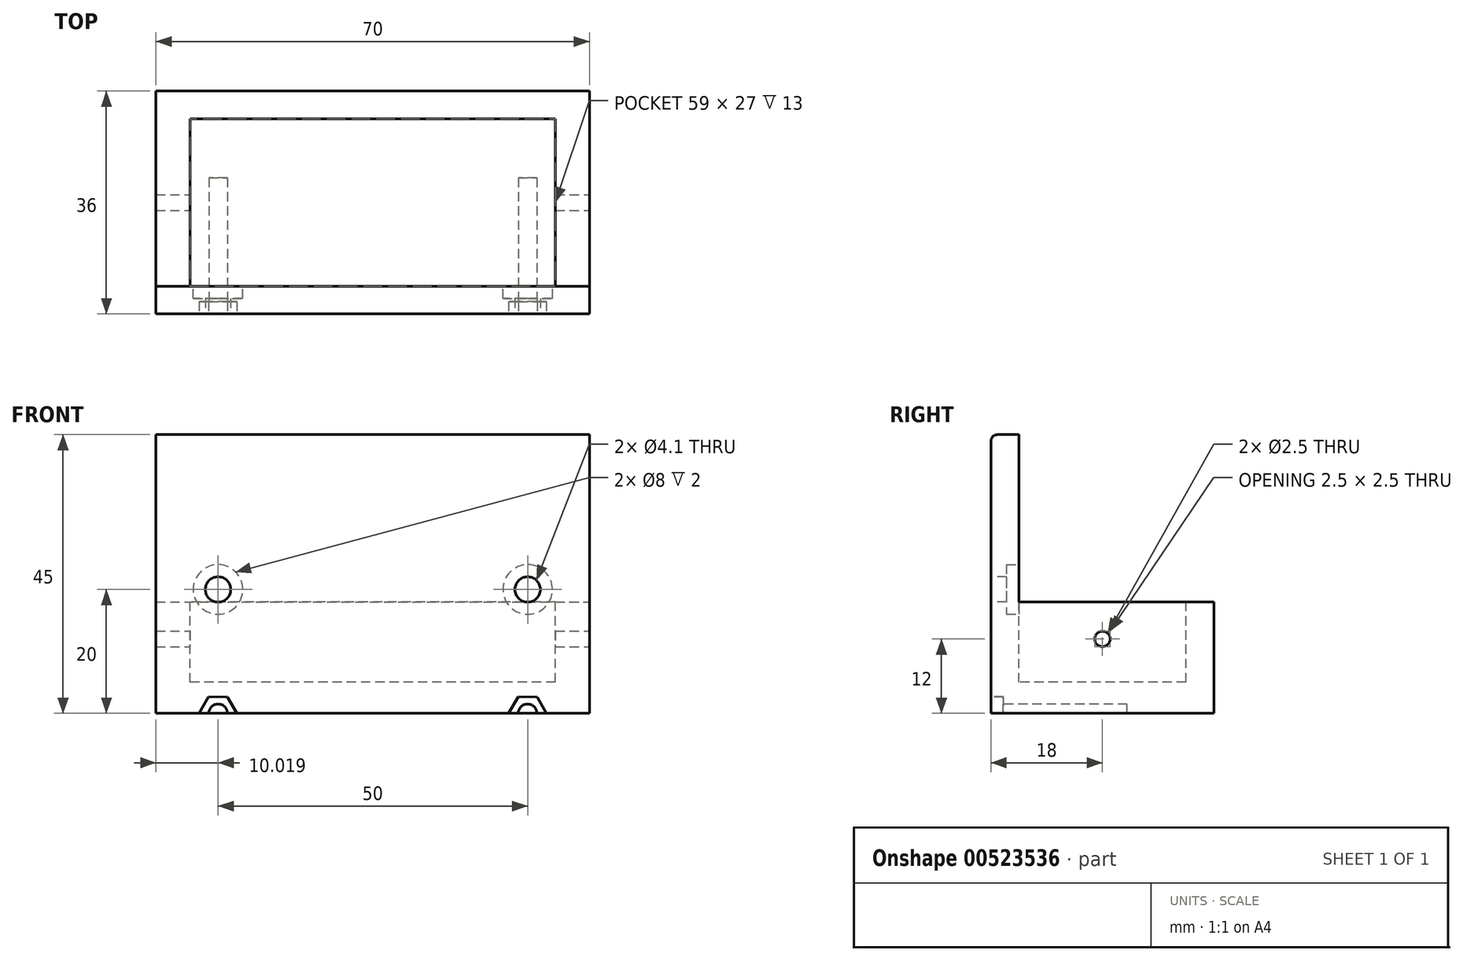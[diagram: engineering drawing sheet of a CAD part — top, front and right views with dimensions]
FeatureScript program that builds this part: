
annotation { "Feature Type Name" : "Feature", "Feature Type Description" : "" }
export const myFeature = defineFeature(function(context is Context, id is Id, definition is map)
    precondition{}
    {
        {
            var Q0;
            Q0=qCreatedBy(makeId("Top.planeOp"),FACE);
            var sketch = newSketch(context, id + "F0", { "sketchPlane" : qUnion([Q0])});
            skLineSegment(sketch, "E0.bottom", {"start": v(35, 18) * mm, "end": v(-35, 18) * mm});
            skLineSegment(sketch, "E0.top", {"start": v(35, -18) * mm, "end": v(-35, -18) * mm});
            skLineSegment(sketch, "E0.left", {"start": v(35, 18) * mm, "end": v(35, -18) * mm});
            skLineSegment(sketch, "E0.right", {"start": v(-35, 18) * mm, "end": v(-35, -18) * mm});
            skPoint(sketch, "E0.middle", {"position": v(0, 0) * mm});
            skSolve(sketch);
        }
        {
            var Q0;
            Q0=makeQuery(id+"F0.imprint","IMPRINT",FACE,{"disambiguationData":[TD([[makeQuery(id+"F0.imprint","IMPRINT",EDGE,{"derivedFrom":sQuery(id+"F0.wireOp",EDGE,"E0.bottom")}),1.0]])]});
            extrude(context, id + "F1", {"entities" : qUnion([Q0]), "depth" : 45 * mm, "offsetDistance" : 25.4 * mm});
        }
        {
            var Q0;
            Q0=makeQuery(id+"F1.opExtrude","CAP_FACE",FACE,{"disambiguationData":[OSD([sQuery(id+"F0.wireOp",EDGE,"E0.bottom"),sQuery(id+"F0.wireOp",EDGE,"E0.top"),sQuery(id+"F0.wireOp",EDGE,"E0.left"),sQuery(id+"F0.wireOp",EDGE,"E0.right")])],"isStart":false});
            var sketch = newSketch(context, id + "F2", { "sketchPlane" : qUnion([Q0])});
            skLineSegment(sketch, "E1.bottom", {"start": v(29.5, 13.5) * mm, "end": v(-29.5, 13.5) * mm});
            skLineSegment(sketch, "E1.top", {"start": v(29.5, -13.5) * mm, "end": v(-29.5, -13.5) * mm});
            skLineSegment(sketch, "E1.left", {"start": v(29.5, 13.5) * mm, "end": v(29.5, -13.5) * mm});
            skLineSegment(sketch, "E1.right", {"start": v(-29.5, 13.5) * mm, "end": v(-29.5, -13.5) * mm});
            skPoint(sketch, "E1.middle", {"position": v(0, 0) * mm});
            skSolve(sketch);
        }
        {
            var Q0;
            Q0=makeQuery(id+"F2.imprint","IMPRINT",FACE,{"disambiguationData":[TD([[makeQuery(id+"F2.imprint","IMPRINT",EDGE,{"derivedFrom":sQuery(id+"F2.wireOp",EDGE,"E1.bottom")}),1.0]])]});
            extrude(context, id + "F3", {"entities" : qUnion([Q0]), "operationType" : NewBodyOperationType.REMOVE, "oppositeDirection" : true, "depth" : 40 * mm, "offsetDistance" : 25.4 * mm});
        }
        {
            var Q0;
            Q0=makeQuery(id+"F1.opExtrude","SWEPT_FACE",FACE,{"disambiguationData":[OSD([sQuery(id+"F0.wireOp",EDGE,"E0.left")])]});
            var sketch = newSketch(context, id + "F4", { "sketchPlane" : qUnion([Q0])});
            skLineSegment(sketch, "E2.bottom", {"start": v(-13.5, 45) * mm, "end": v(18.02, 45) * mm});
            skLineSegment(sketch, "E2.top", {"start": v(-13.5, 18) * mm, "end": v(18.02, 18) * mm});
            skLineSegment(sketch, "E2.left", {"start": v(-13.5, 45) * mm, "end": v(-13.5, 18) * mm});
            skLineSegment(sketch, "E2.right", {"start": v(18.02, 45) * mm, "end": v(18.02, 18) * mm});
            skSolve(sketch);
        }
        {
            var Q0;
            Q0=makeQuery(id+"F4.imprint","IMPRINT",FACE,{"disambiguationData":[TD([[makeQuery(id+"F4.imprint","IMPRINT",EDGE,{"derivedFrom":sQuery(id+"F4.wireOp",EDGE,"E2.bottom")}),1.0]])]});
            extrude(context, id + "F5", {"entities" : qUnion([Q0]), "operationType" : NewBodyOperationType.REMOVE, "endBound" : BoundingType.THROUGH_ALL, "oppositeDirection" : true, "depth" : 25.4 * mm, "offsetDistance" : 25.4 * mm});
        }
        {
            var Q0;
            Q0=makeQuery(id+"F1.opExtrude","SWEPT_FACE",FACE,{"disambiguationData":[OSD([sQuery(id+"F0.wireOp",EDGE,"E0.left")])]});
            var sketch = newSketch(context, id + "F6", { "sketchPlane" : qUnion([Q0])});
            skCircle(sketch, "E3", {"center": v(0, 12) * mm, "radius": 1.25 * mm});
            skSolve(sketch);
        }
        {
            var Q0;
            Q0=makeQuery(id+"F6.imprint","IMPRINT",FACE,{"disambiguationData":[TD([[makeQuery(id+"F6.imprint","IMPRINT",EDGE,{"derivedFrom":sQuery(id+"F6.wireOp",EDGE,"E3")}),1.0]])]});
            extrude(context, id + "F7", {"entities" : qUnion([Q0]), "operationType" : NewBodyOperationType.REMOVE, "endBound" : BoundingType.THROUGH_ALL, "oppositeDirection" : true, "depth" : 25.4 * mm, "offsetDistance" : 25.4 * mm});
        }
        {
            var Q0;
            Q0=makeQuery(id+"F1.opExtrude","SWEPT_FACE",FACE,{"disambiguationData":[OSD([sQuery(id+"F0.wireOp",EDGE,"E0.top")])]});
            var sketch = newSketch(context, id + "F8", { "sketchPlane" : qUnion([Q0])});
            skPoint(sketch, "E4", {"position": v(0, 0) * mm});
            skCircle(sketch, "E5.cCircle", {"center": v(25, 0) * mm, "radius": 2.64 * mm, "construction": true});
            skLineSegment(sketch, "E5.0", {"start": v(23.46, -2.63) * mm, "end": v(21.95, 0.02) * mm});
            skLineSegment(sketch, "E5.1", {"start": v(21.95, 0.02) * mm, "end": v(23.5, 2.65) * mm});
            skLineSegment(sketch, "E5.2", {"start": v(23.5, 2.65) * mm, "end": v(26.54, 2.63) * mm});
            skLineSegment(sketch, "E5.3", {"start": v(26.54, 2.63) * mm, "end": v(28.05, -0.02) * mm});
            skLineSegment(sketch, "E5.4", {"start": v(28.05, -0.02) * mm, "end": v(26.5, -2.65) * mm});
            skLineSegment(sketch, "E5.5", {"start": v(26.5, -2.65) * mm, "end": v(23.46, -2.63) * mm});
            skPoint(sketch, "E5.0.midPoint", {"position": v(22.7, -1.3) * mm});
            skCircle(sketch, "E6.cCircle", {"center": v(-25, 0) * mm, "radius": 2.64 * mm, "construction": true});
            skLineSegment(sketch, "E6.0", {"start": v(-26.54, -2.63) * mm, "end": v(-28.05, 0.02) * mm});
            skLineSegment(sketch, "E6.1", {"start": v(-28.05, 0.02) * mm, "end": v(-26.5, 2.65) * mm});
            skLineSegment(sketch, "E6.2", {"start": v(-26.5, 2.65) * mm, "end": v(-23.46, 2.63) * mm});
            skLineSegment(sketch, "E6.3", {"start": v(-23.46, 2.63) * mm, "end": v(-21.95, -0.02) * mm});
            skLineSegment(sketch, "E6.4", {"start": v(-21.95, -0.02) * mm, "end": v(-23.5, -2.65) * mm});
            skLineSegment(sketch, "E6.5", {"start": v(-23.5, -2.65) * mm, "end": v(-26.54, -2.63) * mm});
            skPoint(sketch, "E6.0.midPoint", {"position": v(-27.3, -1.3) * mm});
            skSolve(sketch);
        }
        {
            var Q0;
            {var subQ6=sQuery(id+"F8.wireOp",EDGE,"E6.1");Q0=makeQuery(id+"F8.imprint","IMPRINT",FACE,{"disambiguationData":[TD([[makeQuery(id+"F8.imprint","IMPRINT",EDGE,{"derivedFrom":subQ6}),-1.0]])]});}
            var Q1;
            {var subQ4=sQuery(id+"F8.wireOp",EDGE,"E5.1");Q1=makeQuery(id+"F8.imprint","IMPRINT",FACE,{"disambiguationData":[TD([[makeQuery(id+"F8.imprint","IMPRINT",EDGE,{"derivedFrom":subQ4}),-1.0]])]});}
            extrude(context, id + "F9", {"entities" : qUnion([Q0, Q1]), "operationType" : NewBodyOperationType.REMOVE, "oppositeDirection" : true, "depth" : 2 * mm, "offsetDistance" : 25.4 * mm});
        }
        {
            var Q0;
            Q0=makeQuery(id+"F9.boolean.opBoolean","COPY",FACE,{"derivedFrom":makeQuery(id+"F9.opExtrude","CAP_FACE",FACE,{"disambiguationData":[OSD([sQuery(id+"F0.wireOp",EDGE,"E0.top"),sQuery(id+"F8.wireOp",EDGE,"E5.0"),sQuery(id+"F8.wireOp",EDGE,"E5.1"),sQuery(id+"F8.wireOp",EDGE,"E5.2"),sQuery(id+"F8.wireOp",EDGE,"E5.3")])],"isStart":false})});
            var sketch = newSketch(context, id + "F10", { "sketchPlane" : qUnion([Q0])});
            skCircle(sketch, "E7", {"center": v(25, 0) * mm, "radius": 1.5 * mm});
            skCircle(sketch, "E8", {"center": v(-24.97, 0) * mm, "radius": 1.5 * mm});
            skSolve(sketch);
        }
        {
            var Q0;
            {var subQ0=sQuery(id+"F10.wireOp",EDGE,"E7");var subQ1=sQuery(id+"F0.wireOp",EDGE,"E0.top");var subQ2=makeQuery(id+"F1.opExtrude","CAP_EDGE",EDGE,{"disambiguationData":[OSD([subQ1])],"isStart":true});var subQ3=makeQuery(id+"F9.boolean.opBoolean","COPY",EDGE,{"derivedFrom":makeQuery(id+"F9.opExtrude","CAP_EDGE",EDGE,{"disambiguationData":[OSD([subQ1]),TDD([makeQuery(id+"F8.imprint","IMPRINT",EDGE,{"disambiguationData":[TD([[makeQuery(id+"F8.imprint","INTERSECT",VERTEX,{"derivedFrom":[subQ2,sQuery(id+"F8.wireOp",EDGE,"E5.0")]}),1.0]])],"derivedFrom":subQ2})])],"isStart":false})});var subQ4=makeQuery(id+"F10.imprint","INTERSECT",VERTEX,{"disambiguationData":[OD(0.0)],"derivedFrom":[subQ3,subQ0]});Q0=makeQuery(id+"F10.imprint","IMPRINT",FACE,{"disambiguationData":[TD([[makeQuery(id+"F10.imprint","IMPRINT",EDGE,{"disambiguationData":[TD([[subQ4,-1.0]])],"derivedFrom":subQ0}),1.0]])]});}
            var Q1;
            {var subQ0=sQuery(id+"F10.wireOp",EDGE,"E7");var subQ1=sQuery(id+"F0.wireOp",EDGE,"E0.top");var subQ2=makeQuery(id+"F1.opExtrude","CAP_EDGE",EDGE,{"disambiguationData":[OSD([subQ1])],"isStart":true});var subQ3=makeQuery(id+"F9.boolean.opBoolean","COPY",EDGE,{"derivedFrom":makeQuery(id+"F9.opExtrude","CAP_EDGE",EDGE,{"disambiguationData":[OSD([subQ1]),TDD([makeQuery(id+"F8.imprint","IMPRINT",EDGE,{"disambiguationData":[TD([[makeQuery(id+"F8.imprint","INTERSECT",VERTEX,{"derivedFrom":[subQ2,sQuery(id+"F8.wireOp",EDGE,"E5.0")]}),1.0]])],"derivedFrom":subQ2})])],"isStart":false})});var subQ4=makeQuery(id+"F10.imprint","INTERSECT",VERTEX,{"disambiguationData":[OD(0.0)],"derivedFrom":[subQ3,subQ0]});Q1=makeQuery(id+"F10.imprint","IMPRINT",FACE,{"disambiguationData":[TD([[makeQuery(id+"F10.imprint","IMPRINT",EDGE,{"disambiguationData":[TD([[subQ4,1.0]])],"derivedFrom":subQ0}),1.0]])]});}
            var Q2;
            Q2=makeQuery(id+"F10.imprint","IMPRINT",FACE,{"disambiguationData":[TD([[makeQuery(id+"F10.imprint","IMPRINT",EDGE,{"derivedFrom":sQuery(id+"F10.wireOp",EDGE,"E8")}),1.0]])]});
            extrude(context, id + "F11", {"entities" : qUnion([Q0, Q1, Q2]), "operationType" : NewBodyOperationType.REMOVE, "oppositeDirection" : true, "depth" : 20 * mm, "offsetDistance" : 25.4 * mm});
        }
        {
            var Q0;
            Q0=makeQuery(id+"F1.opExtrude","SWEPT_FACE",FACE,{"disambiguationData":[OSD([sQuery(id+"F0.wireOp",EDGE,"E0.top")])]});
            var sketch = newSketch(context, id + "F12", { "sketchPlane" : qUnion([Q0])});
            skCircle(sketch, "E9", {"center": v(25.02, 20) * mm, "radius": 2.05 * mm});
            skPoint(sketch, "E9.centerSnap0", {"position": v(25.02, 2.64) * mm});
            skCircle(sketch, "E10", {"center": v(-24.98, 20) * mm, "radius": 2.05 * mm});
            skPoint(sketch, "E11", {"position": v(-24.98, 2.64) * mm});
            skSolve(sketch);
        }
        {
            var Q0;
            Q0=makeQuery(id+"F12.imprint","IMPRINT",FACE,{"disambiguationData":[TD([[makeQuery(id+"F12.imprint","IMPRINT",EDGE,{"derivedFrom":sQuery(id+"F12.wireOp",EDGE,"E10")}),1.0]])]});
            var Q1;
            Q1=makeQuery(id+"F12.imprint","IMPRINT",FACE,{"disambiguationData":[TD([[makeQuery(id+"F12.imprint","IMPRINT",EDGE,{"derivedFrom":sQuery(id+"F12.wireOp",EDGE,"E9")}),1.0]])]});
            extrude(context, id + "F13", {"entities" : qUnion([Q0, Q1]), "operationType" : NewBodyOperationType.REMOVE, "oppositeDirection" : true, "depth" : 25.4 * mm, "offsetDistance" : 25.4 * mm});
        }
        {
            var Q0;
            Q0=makeQuery(id+"F5.boolean.opBoolean","MERGE",FACE,{"derivedFrom":[makeQuery(id+"F3.boolean.opBoolean","COPY",FACE,{"derivedFrom":makeQuery(id+"F3.opExtrude","SWEPT_FACE",FACE,{"disambiguationData":[OSD([sQuery(id+"F2.wireOp",EDGE,"E1.top")])]})}),makeQuery(id+"F5.opExtrude","SWEPT_FACE",FACE,{"disambiguationData":[OSD([sQuery(id+"F4.wireOp",EDGE,"E2.left")])]})]});
            var sketch = newSketch(context, id + "F14", { "sketchPlane" : qUnion([Q0])});
            skCircle(sketch, "E12", {"center": v(24.98, 20) * mm, "radius": 4 * mm});
            skCircle(sketch, "E13", {"center": v(-25.02, 20) * mm, "radius": 4 * mm});
            skSolve(sketch);
        }
        {
            var Q0;
            Q0=makeQuery(id+"F14.imprint","IMPRINT",FACE,{"disambiguationData":[TD([[makeQuery(id+"F14.imprint","IMPRINT",EDGE,{"derivedFrom":sQuery(id+"F14.wireOp",EDGE,"E12")}),1.0]])]});
            var Q1;
            Q1=makeQuery(id+"F14.imprint","IMPRINT",FACE,{"disambiguationData":[TD([[makeQuery(id+"F14.imprint","IMPRINT",EDGE,{"derivedFrom":sQuery(id+"F14.wireOp",EDGE,"E13")}),1.0]])]});
            extrude(context, id + "F15", {"entities" : qUnion([Q0, Q1]), "operationType" : NewBodyOperationType.REMOVE, "oppositeDirection" : true, "depth" : 2 * mm, "offsetDistance" : 25.4 * mm});
        }
        {
            var Q0;
            Q0=makeQuery(id+"F5.boolean.opBoolean","MERGE",EDGE,{"derivedFrom":[makeQuery(id+"F3.boolean.opBoolean","COPY",EDGE,{"derivedFrom":makeQuery(id+"F3.opExtrude","CAP_EDGE",EDGE,{"disambiguationData":[OSD([sQuery(id+"F2.wireOp",EDGE,"E1.bottom")])],"isStart":true})}),makeQuery(id+"F5.opExtrude","SWEPT_EDGE",EDGE,{"disambiguationData":[OSD([sQuery(id+"F0.wireOp",EDGE,"E0.left"),sQuery(id+"F4.wireOp",EDGE,"E2.bottom"),sQuery(id+"F4.wireOp",EDGE,"E2.right")])]})]});
            var Q1;
            Q1=makeQuery(id+"F1.opExtrude","CAP_EDGE",EDGE,{"disambiguationData":[OSD([sQuery(id+"F0.wireOp",EDGE,"E0.bottom")])],"isStart":false});
            var Q2;
            Q2=makeQuery(id+"F5.boolean.opBoolean","MERGE",EDGE,{"derivedFrom":[makeQuery(id+"F3.boolean.opBoolean","COPY",EDGE,{"derivedFrom":makeQuery(id+"F3.opExtrude","CAP_EDGE",EDGE,{"disambiguationData":[OSD([sQuery(id+"F2.wireOp",EDGE,"E1.top")])],"isStart":true})}),makeQuery(id+"F5.opExtrude","SWEPT_EDGE",EDGE,{"disambiguationData":[OSD([sQuery(id+"F0.wireOp",EDGE,"E0.left"),sQuery(id+"F4.wireOp",EDGE,"E2.bottom"),sQuery(id+"F4.wireOp",EDGE,"E2.left")])]})]});
            var Q3;
            Q3=makeQuery(id+"F1.opExtrude","CAP_EDGE",EDGE,{"disambiguationData":[OSD([sQuery(id+"F0.wireOp",EDGE,"E0.top")])],"isStart":false});
            fillet(context, id + "F16", {"entities" : qUnion([Q0, Q1, Q2, Q3]), "radius" : 1 * mm, "tangentPropagation" : true, "allowEdgeOverflow" : false});
        }
    });
